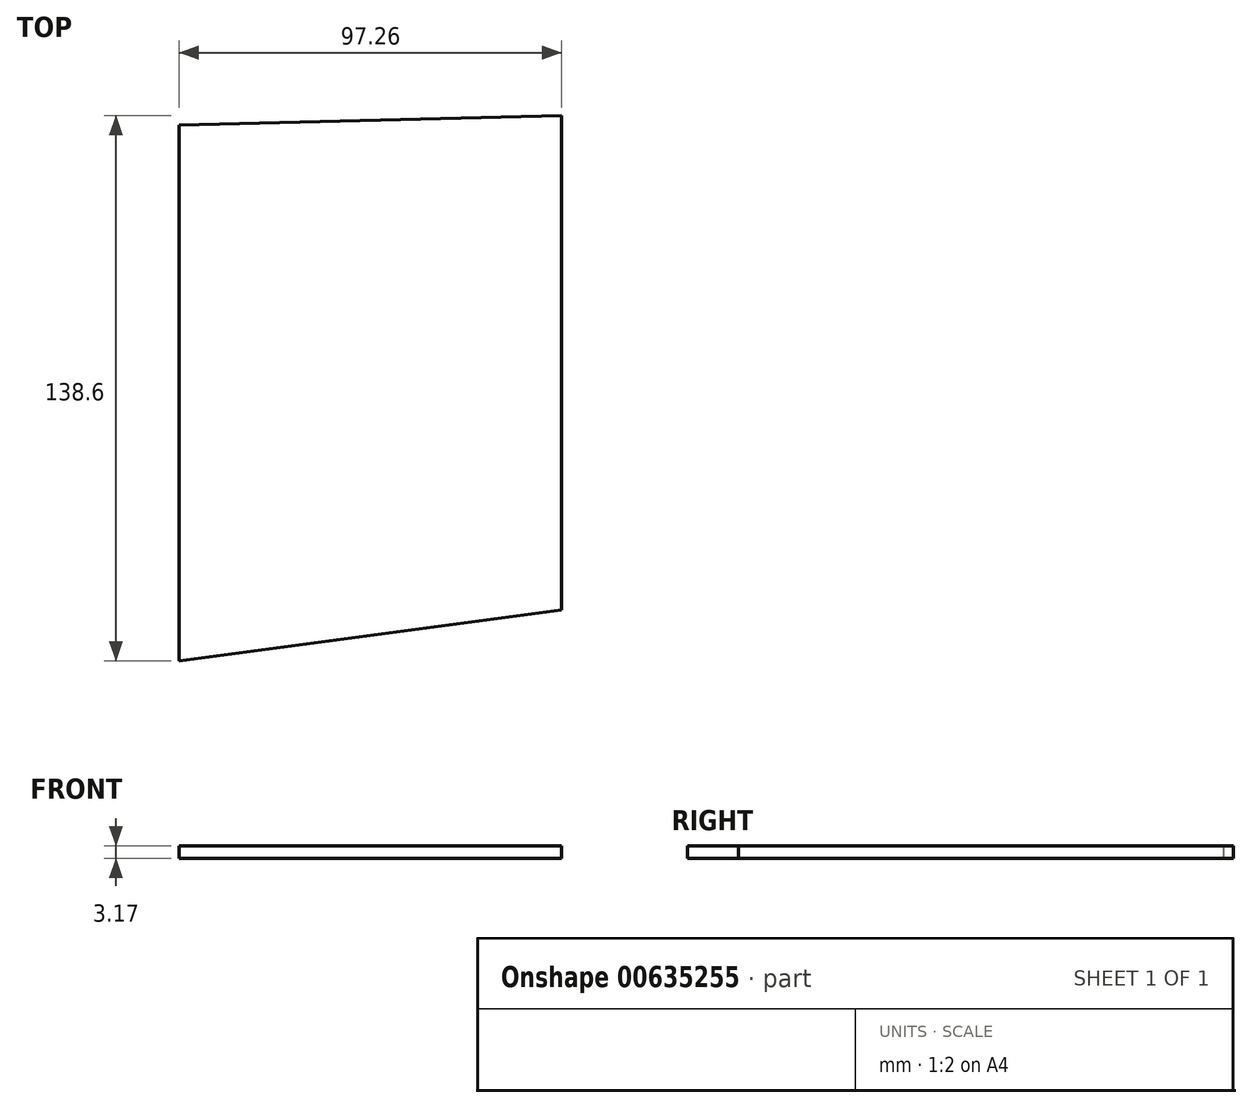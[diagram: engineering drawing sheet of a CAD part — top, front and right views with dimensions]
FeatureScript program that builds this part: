
annotation { "Feature Type Name" : "Feature", "Feature Type Description" : "" }
export const myFeature = defineFeature(function(context is Context, id is Id, definition is map)
    precondition{}
    {
        {
            var Q0;
            Q0=qCreatedBy(makeId("Top.planeOp"),FACE);
            var sketch = newSketch(context, id + "F0", { "sketchPlane" : qUnion([Q0])});
            skLineSegment(sketch, "E0.bottom", {"start": v(0, 0) * mm, "end": v(-97.26, 0) * mm});
            skLineSegment(sketch, "E0.left", {"start": v(0, 12.95) * mm, "end": v(0, 138.6) * mm});
            skLineSegment(sketch, "E0.right", {"start": v(-97.26, 0) * mm, "end": v(-97.26, 136.1) * mm});
            skLineSegment(sketch, "E1", {"start": v(-97.26, 0) * mm, "end": v(0, 12.95) * mm});
            skLineSegment(sketch, "E2", {"start": v(0, 138.6) * mm, "end": v(-97.26, 136.1) * mm});
            skPoint(sketch, "E3.orphan", {"position": v(0, 210.82) * mm});
            skSolve(sketch);
        }
        {
            var Q0;
            Q0 = qSketchRegion(id + "F0", true);
            extrude(context, id + "F1", {"entities" : qUnion([Q0]), "depth" : 3.17 * mm, "offsetDistance" : 25.4 * mm});
        }
    });
